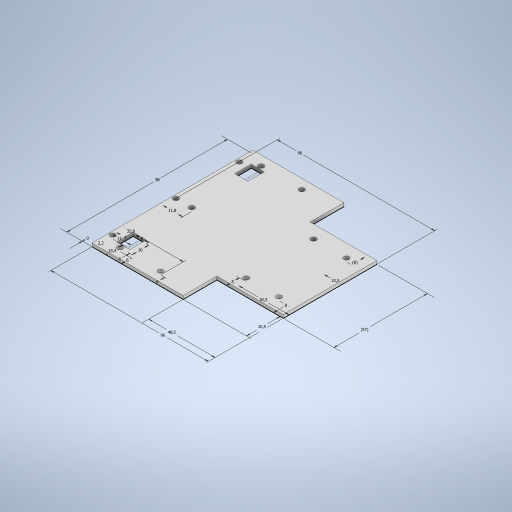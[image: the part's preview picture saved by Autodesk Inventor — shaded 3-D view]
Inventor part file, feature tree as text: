
AUTODESK INVENTOR PART (.ipt)
format: ipt  version: 2023 (Build 270158000, 158)  size: 295,936 bytes
history: native  units: in
note: dims shown in document units (in); Inventor stores cm internally (conversion verified against a paired STEP export)
features: hole x5, extrude x2, other x1, sketch x1
ambient origin geometry x8: Origin, YZ Plane, XZ Plane, XY Plane, X Axis, Y Axis, Z Axis, Center Point
bodies: Body1 (feature_tree)
feature tree (9):
  other  "Bryła1"
  sketch  "Szkic1"
  extrude  "Wyciągnięcie proste1"  Depth=3.8583in
  hole  "Hole4"  [1 undecoded]
  hole  "Otwór5"  [1 undecoded]
  hole  "Hole6"  [1 undecoded]
  hole  "Hole7"  [1 undecoded]
  hole  "Hole8"  [1 undecoded]
  extrude  "Extrusion2"  Depth=0.4094in
note: 5 required parameter values undecoded (feature->parameter linkage not recoverable at this tier; creation-order binding heuristic only, values carry confidence <= 0.55)
